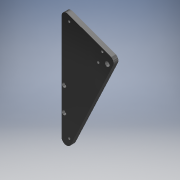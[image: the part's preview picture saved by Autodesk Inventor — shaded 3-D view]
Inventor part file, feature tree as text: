
AUTODESK INVENTOR PART (.ipt)
format: ipt  version: 2019 (Build 230136000, 136)  size: 151,040 bytes
history: native  units: mm (DEFAULTED — no unit token found)
features: sketch x6, extrude x5, fillet x2, hole x1
ambient origin geometry x8: Origin, YZ Plane, XZ Plane, XY Plane, X Axis, Y Axis, Z Axis, Center Point
bodies: Solid1 (feature_tree)
feature tree (14):
  extrude  "Extrusion1"  Depth=6.35mm TaperAngle=0.0deg
  fillet  "Fillet1"  Radius=6.35mm
  fillet  "Fillet4"  Radius=76.2mm
  extrude  "Extrusion3"  Depth=6.35mm
  extrude  "Extrusion4"  Depth=3.048mm
  extrude  "Extrusion5"  Depth=3.175mm
  hole  "Hole1"  [1 undecoded]
  extrude  "Extrusion6"  Depth=3.175mm
  sketch  "Sketch1"  dims[d0=177.8mm d2=6.35mm d3=0.0mm d4=6.35mm d19=76.2mm]
  sketch  "Sketch3"  dims[d20=3.490659mm d21=6.35mm]
  sketch  "Sketch4"  dims[d22=3.048mm d23=3.048mm]
  sketch  "Sketch5"  dims[d24=3.175mm d25=3.175mm]
  sketch  "Sketch6"  dims[d26=29.845mm d27=31.75mm]
  sketch  "Sketch7"  dims[d28=25.4mm d29=0.0mm d30=5.842mm d31=5.842mm d32=3.556mm d33=0.0mm d34=6.35mm d35=52.2732mm d36=31.5976mm d37=25.4mm d38=0.0mm d39=10.0076mm d40=1.905mm d41=136.906mm d42=0.0mm d43=3.0mm d44=19.05mm d45=9.525mm d46=6.35mm d47=14.3117mm d48=25.4mm d49=20.594885mm d52=3.81mm d53=19.812mm d54=15.3162mm d55=16.8656mm d56=3.175mm d57=3.175mm d58=25.4mm d59=0.0mm]
note: 1 required parameter value undecoded (feature->parameter linkage not recoverable at this tier; creation-order binding heuristic only, values carry confidence <= 0.55)
